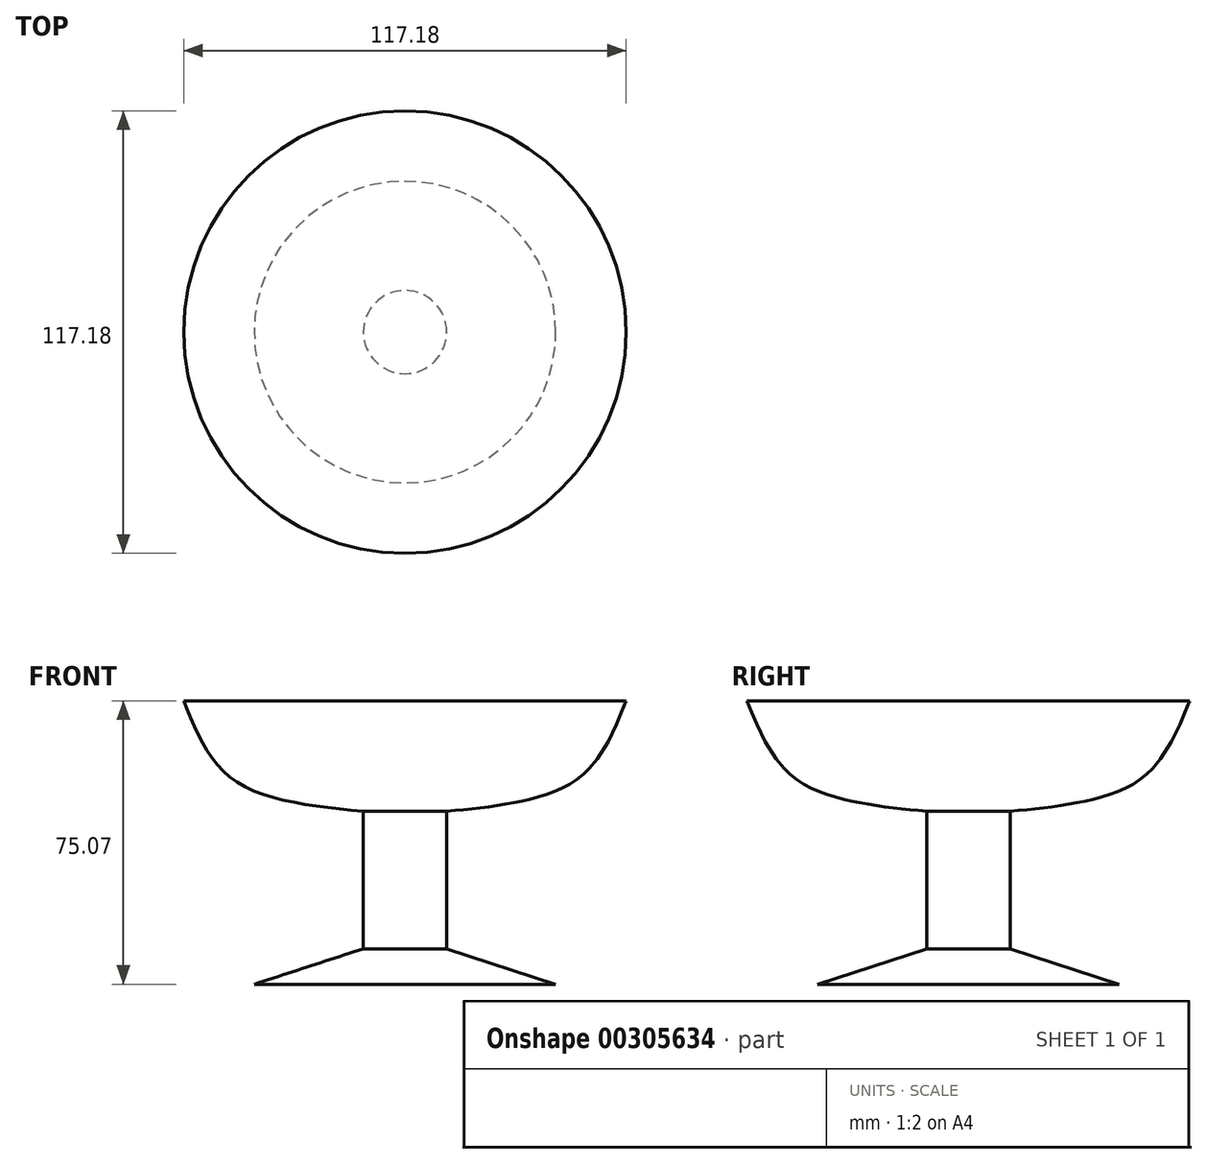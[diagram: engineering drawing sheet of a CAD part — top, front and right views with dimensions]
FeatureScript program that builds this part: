
annotation { "Feature Type Name" : "Feature", "Feature Type Description" : "" }
export const myFeature = defineFeature(function(context is Context, id is Id, definition is map)
    precondition{}
    {
        {
            var Q0;
            Q0=qCreatedBy(makeId("Front.planeOp"),FACE);
            var sketch = newSketch(context, id + "F0", { "sketchPlane" : qUnion([Q0])});
            skLineSegment(sketch, "E0", {"start": v(0, 0) * mm, "end": v(0, 75.07) * mm});
            skLineSegment(sketch, "E1", {"start": v(0, 75.07) * mm, "end": v(58.59, 75.07) * mm});
            skLineSegment(sketch, "E2", {"start": v(0, 0) * mm, "end": v(39.92, 0) * mm});
            skLineSegment(sketch, "E3", {"start": v(39.92, 0) * mm, "end": v(11.04, 9.4) * mm});
            skLineSegment(sketch, "E4", {"start": v(11.04, 9.4) * mm, "end": v(11.04, 45.78) * mm});
            skFitSpline(sketch, "E5", {"points": [v(11.04, 45.78) * mm, v(45.5, 54.23) * mm, v(58.59, 75.07) * mm], "startDerivative": vector(72.56, 7.19) * mm, "endDerivative": vector(20.97, 52.78) * mm});
            skSolve(sketch);
        }
        {
            var Q0;
            Q0 = qSketchRegion(id + "F0", true);
            var Q1;
            Q1=sQuery(id+"F0.wireOp",EDGE,"E0");
            revolve(context, id + "F1", {"entities" : qUnion([Q0]), "axis" : qUnion([Q1]), "revolveType" : RevolveType.FULL});
        }
    });
